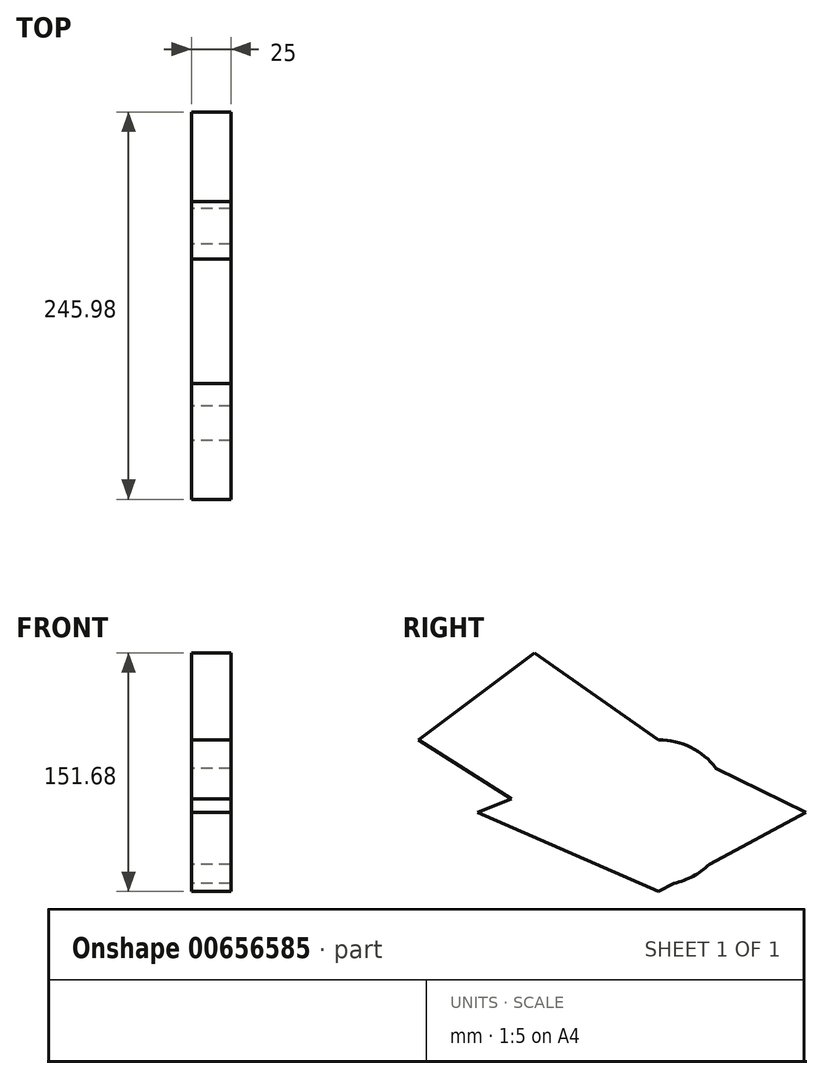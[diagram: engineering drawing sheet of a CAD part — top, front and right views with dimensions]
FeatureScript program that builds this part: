
annotation { "Feature Type Name" : "Feature", "Feature Type Description" : "" }
export const myFeature = defineFeature(function(context is Context, id is Id, definition is map)
    precondition{}
    {
        {
            var Q0;
            Q0=qCreatedBy(makeId("Right.planeOp"),FACE);
            var sketch = newSketch(context, id + "F0", { "sketchPlane" : qUnion([Q0])});
            skCircle(sketch, "E0", {"center": v(0, 0) * mm, "radius": 46.07 * mm});
            skLineSegment(sketch, "E1", {"start": v(0, 46.07) * mm, "end": v(-115.2, 0) * mm});
            skLineSegment(sketch, "E2", {"start": v(-115.2, 0) * mm, "end": v(0, -50.26) * mm});
            skLineSegment(sketch, "E3", {"start": v(0, -50.26) * mm, "end": v(93.54, 0) * mm});
            skLineSegment(sketch, "E4", {"start": v(93.54, 0) * mm, "end": v(0, 46.07) * mm});
            skLineSegment(sketch, "E5", {"start": v(-78.82, 101.42) * mm, "end": v(-152.44, 46.07) * mm});
            skLineSegment(sketch, "E6", {"start": v(-152.44, 46.07) * mm, "end": v(0, -50.26) * mm});
            skLineSegment(sketch, "E7", {"start": v(0, 46.07) * mm, "end": v(-78.82, 101.42) * mm});
            skSolve(sketch);
        }
        {
            var Q0;
            Q0 = qSketchRegion(id + "F0", true);
            extrude(context, id + "F1", {"entities" : qUnion([Q0]), "depth" : 25 * mm, "offsetDistance" : 25 * mm});
        }
    });
